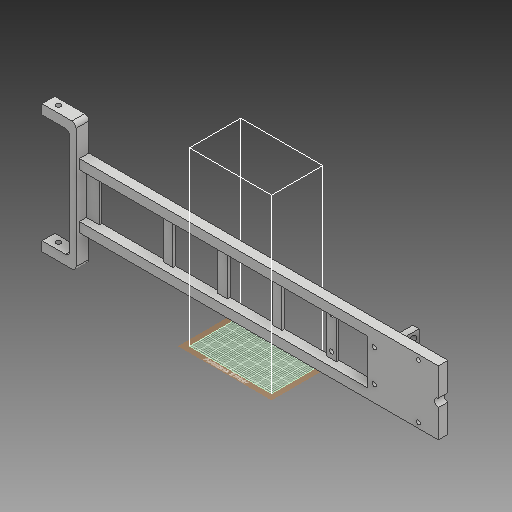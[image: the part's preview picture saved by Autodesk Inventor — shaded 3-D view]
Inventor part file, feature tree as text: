
AUTODESK INVENTOR PART (.ipt)
format: ipt  version: 2019 (Build 230136000, 136)  size: 619,008 bytes
history: native  units: mm
features: sketch x32, extrude x25, fillet x6, hole x5
ambient origin geometry x8: Origin, YZ Plane, XZ Plane, XY Plane, X Axis, Y Axis, Z Axis, Center Point
bodies: Solid1 (feature_tree)
feature tree (68):
  extrude  "Extrusion1"  Depth=50.0mm
  hole  "Hole1"  [1 undecoded]
  hole  "Hole2"  [1 undecoded]
  extrude  "Extrusion2"  Depth=25.0mm
  extrude  "Extrusion3"  Depth=25.0mm
  extrude  "Extrusion4"  Depth=5.0mm
  sketch  "Sketch7"  dims[d25=10.0mm d26=5.0mm]
  extrude  "Extrusion5"  Depth=5.0mm
  extrude  "Extrusion6"  Depth=35.0mm
  extrude  "Extrusion7"  Depth=35.0mm
  extrude  "Extrusion8"  Depth=35.0mm
  extrude  "Extrusion9"  Depth=2.0mm TaperAngle=0.0deg
  extrude  "Extrusion10"  Depth=7.5mm TaperAngle=0.0deg
  extrude  "Extrusion11"  Depth=10.0mm
  extrude  "Extrusion12"  Depth=7.5mm
  fillet  "Fillet1"  Radius=7.5mm
  fillet  "Fillet2"  Radius=25.0mm
  fillet  "Fillet3"  Radius=3.0mm
  fillet  "Fillet4"  Radius=3.2mm
  fillet  "Fillet5"  Radius=2.1mm
  fillet  "Fillet6"  Radius=5.5mm
  extrude  "Extrusion13"  Depth=92.5mm TaperAngle=0.0deg
  sketch  "Sketch17"  dims[d58=4.25mm d59=241.0mm d60=0.0mm]
  hole  "Hole3"  [1 undecoded]
  hole  "Hole4"  [1 undecoded]
  extrude  "Extrusion14"  Depth=5.0mm
  extrude  "Extrusion15"  Depth=2.5mm TaperAngle=0.0deg
  extrude  "Extrusion16"  Depth=6.35mm
  extrude  "Extrusion17"  Depth=2.5mm
  extrude  "Extrusion18"  Depth=14.55mm TaperAngle=0.0deg
  extrude  "Extrusion19"  Depth=0.1mm
  extrude  "Extrusion20"  Depth=3.25mm
  extrude  "Extrusion21"  Depth=3.25mm
  hole  "Hole5"  [1 undecoded]
  extrude  "Extrusion22"  Depth=2.0mm
  extrude  "Extrusion23"  Depth=15.0mm
  extrude  "Extrusion24"  Depth=10.0mm TaperAngle=0.0deg
  extrude  "Extrusion25"  Depth=4.0mm
  sketch  "Sketch1"  dims[d0=50.0mm d1=50.0mm]
  sketch  "Sketch2"  dims[d2=240.0mm d3=7.5mm]
  sketch  "Sketch3"  dims[d4=7.5mm d5=7.5mm d6=0.0mm]
  sketch  "Sketch4"  dims[d7=6.35mm d8=6.0mm d9=4.0mm d10=2.0mm d11=90.0deg d12=8.0mm d13=20.594885mm d14=25.0mm]
  sketch  "Sketch5"  dims[d15=3.3mm d16=6.0mm d17=4.0mm d18=2.0mm d19=90.0deg d20=8.0mm d21=20.594885mm d22=25.0mm]
  sketch  "Sketch6"  dims[d23=180.0deg d24=5.0mm]
  sketch  "Sketch8"  dims[d27=17.5mm d28=0.0mm d30=35.0mm]
  sketch  "Sketch9"  dims[d31=35.0mm d32=35.0mm]
  sketch  "Sketch10"  dims[d33=35.0mm d34=35.0mm]
  sketch  "Sketch11"  dims[d35=35.0mm d36=2.0mm d37=0.0mm]
  sketch  "Sketch12"  dims[d38=10.0mm d39=7.5mm d40=0.0mm]
  sketch  "Sketch13"  dims[d41=100.0mm d42=10.0mm]
  sketch  "Sketch14"  dims[d43=7.5mm d44=0.0mm d45=7.5mm d46=7.5mm d47=25.0mm d48=0.0mm d49=3.0mm d50=3.2mm d51=2.1mm d52=5.5mm]
  sketch  "Sketch15"  dims[d53=3.3mm d54=92.5mm d55=0.0mm]
  sketch  "Sketch16"  dims[d56=5.5mm d57=3.3mm]
  sketch  "Sketch18"  dims[d61=4.44mm d62=5.0mm]
  sketch  "Sketch19"  dims[d63=2.5mm d64=91.25mm d65=0.0mm]
  sketch  "Sketch20"  dims[d66=30.0mm d67=6.35mm]
  sketch  "Sketch21"  dims[d68=3.8mm d69=0.0mm d70=2.5mm]
  sketch  "Sketch22"  dims[d71=14.55mm d72=0.0mm d73=14.55mm d74=0.0mm]
  sketch  "Sketch23"  dims[d75=0.1mm d76=0.1mm]
  sketch  "Sketch24"  dims[d77=3.25mm d78=3.25mm]
  sketch  "Sketch25"  dims[d79=3.25mm d80=3.25mm]
  sketch  "Sketch26"  dims[d81=35.0mm d82=10.0mm]
  sketch  "Sketch27"  dims[d83=2.0mm d84=0.0mm d85=3.6mm]
  sketch  "Sketch28"  dims[d86=3.6mm]
  sketch  "Sketch29"  dims[d87=3.3mm d88=6.0mm d89=4.0mm d90=2.0mm d91=90.0deg d92=15.0mm d93=20.594885mm]
  sketch  "Sketch30"  dims[d94=3.3mm d95=6.0mm d96=4.0mm d97=2.0mm d98=90.0deg d99=15.0mm d100=20.594885mm d101=6.0mm]
  sketch  "Sketch31"  dims[d102=20.0mm d103=0.0mm d104=10.0mm d105=0.0mm]
  sketch  "Sketch32"  dims[d106=2.0mm d107=0.0mm d108=4.0mm d109=100.0mm d110=0.0mm d111=100.0mm d112=0.0mm d113=5.0mm d114=2.0mm d115=0.0mm d116=3.3mm d117=3.3mm d118=3.3mm d119=3.3mm d120=2.0mm d121=0.0mm d122=5.5mm d123=0.0mm d124=3.3mm d125=6.0mm d126=4.0mm d127=2.0mm d128=90.0deg d129=8.0mm d130=20.594885mm d131=42.0mm d132=17.0mm d133=21.0mm d135=8.5mm d136=15.825mm d137=3.5mm d138=21.0mm d139=3.3mm d140=3.3mm d141=3.3mm d142=10.0mm d143=0.0mm d144=7.5mm d145=0.0mm d146=100.0mm d147=0.0mm d148=4.0mm d149=4.0mm d150=4.0mm d151=4.0mm d152=10.0mm d153=0.0mm]
note: 5 required parameter values undecoded (feature->parameter linkage not recoverable at this tier; creation-order binding heuristic only, values carry confidence <= 0.55)
